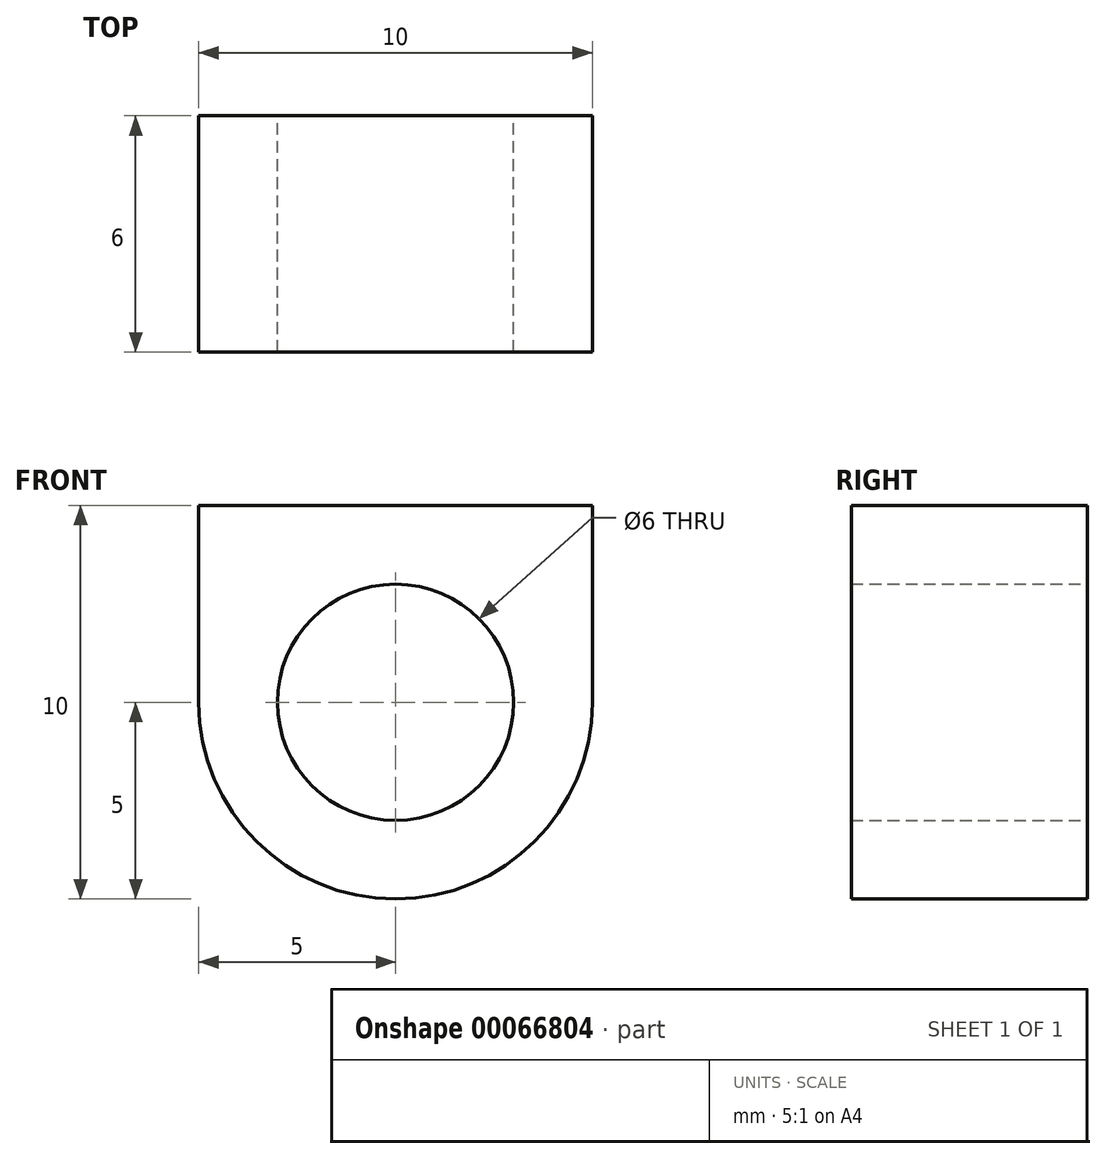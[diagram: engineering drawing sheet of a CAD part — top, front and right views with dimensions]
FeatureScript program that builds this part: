
annotation { "Feature Type Name" : "Feature", "Feature Type Description" : "" }
export const myFeature = defineFeature(function(context is Context, id is Id, definition is map)
    precondition{}
    {
        {
            var Q0;
            Q0=qCreatedBy(makeId("Front.planeOp"),FACE);
            var sketch = newSketch(context, id + "F0", { "sketchPlane" : qUnion([Q0])});
            skCircle(sketch, "E0", {"center": v(0, 0) * mm, "radius": 3 * mm});
            skLineSegment(sketch, "E1", {"start": v(0, 0) * mm, "end": v(0, 0.74) * mm});
            skLineSegment(sketch, "E2", {"start": v(-5, 0) * mm, "end": v(-5, 5) * mm});
            skLineSegment(sketch, "E3", {"start": v(-5, 5) * mm, "end": v(5, 5) * mm});
            skLineSegment(sketch, "E4", {"start": v(5, 5) * mm, "end": v(5, 0) * mm});
            skArc(sketch, "E5", {"start": v(-5, 0) * mm, "mid": v(0, -5) * mm, "end": v(5, 0) * mm});
            skSolve(sketch);
        }
        {
            var Q0;
            Q0=makeQuery(id+"F0.imprint","IMPRINT",FACE,{"disambiguationData":[TD([[makeQuery(id+"F0.imprint","IMPRINT",EDGE,{"derivedFrom":sQuery(id+"F0.wireOp",EDGE,"E0")}),-1.0]])]});
            extrude(context, id + "F1", {"entities" : qUnion([Q0]), "depth" : 6 * mm});
        }
    });
